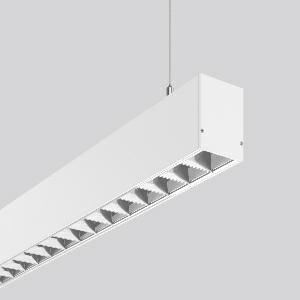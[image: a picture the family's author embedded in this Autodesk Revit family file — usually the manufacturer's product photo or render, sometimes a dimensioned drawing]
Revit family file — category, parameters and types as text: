
# Revit family: less_is_more_50_312341_002_76_e695
name_source: partatom
category: Lighting Fixtures
units: mm (PartAtom-declared; Revit-internal decimal feet)

## family parameters
Cut with Voids When Loaded = No
Host = Face
Light Source = No
Part Type = Normal
Room Calculation Point = No
Round Connector Dimension = Use Diameter
Shared = No

## types (1)
- LESS IS MORE 50 (1 x LED Modul 830, 3950 lm, 3000)
    Apparent Load = 35 VA
    CIE Flux Codes = 95 100 100 63 100
    Color Rendering = 80
    Color Temperature = 3000
    Default Elevation = 1800 mm
    Description = Series: LESS IS MORE 50
Linear pendant luminaire for aesthetically sophisticated lighting. Housing: extruded aluminium profile, powder-coated. End cap aluminium powder-coated. Canopy made of aluminium, powder-coated. Alea optical system: Reflector structure (ABS, Aluminium-coated, highly polished) with integrated diffuser made of non-yellowing plastic (PMMA) opal for glare-free light at the workstation (screen-compliant according to EN 12464-1). Direct 65%, indirect 35% light emission. Controlled separately. Suitable for pendant. 2-point steel cable suspension freely positionable and infinitely height-adjustable. Special lengths available on request. LED unit with integrated converter interchangeable and removable. Suitable for through-wiring. With sensors or as a safety luminaire on request. 
Colour: traffic white, matt (RAL 9016)
Length: 847 mm
Width: 57 mm
Height: 75 mm
Suspension length: 2000 mm
Lamp: LED
Socket: without socket
Colour temperature: 3000K
Colour rendering index (CRI): 80
Light source: LED
Socket lamp2: Without base
Colour temperature: 3000K
System power: 35 W
Rated luminous flux: 3950 lm
Luminous efficiency: 113 lm/W
Control gear: Converter, dimmable, DALI
Control gear: Converter, dimmable, DALI
Protection class: I
Type of protection: IP 20
    Height = 75 mm
    Lamp = 1 x LED Modul 830
    Lamp Light Flux = 3950 lm
    Lamp count = 1
    Length = 847 mm
    Lifetime = 50000 h
    Luminous efficacy = 113 lm/W
    Manufacturer = RZB
    ModVariant = No
    Model = 312341.002.76
    Mounting Place = Ceiling
    Mounting Type = Pendant
    Number of Poles = 1
    OnlyDefault = Yes
    Power Factor = 1
    Product Name = LESS IS MORE 50
    Product group = Pendant LED linear luminaires
    ProductGroupID = 907
    Protection Class = Protection class I
    Protection Degree = IP 20
    RLX_Detail_Level = 1
    RLX_Emergency_Light_Flux = 0 lm
    RLX_Emergency_Type = 0
    RLX_Emergency_Type_DB = No
    RlxData = <blob elided: 37405 chars, md5=40f86997>
    Socket = socket
    Standby Power = 0 W
    System Light Flux = 3950 lm
    System Power = 35 W
    Type Comments = Product without accessories
    Type Image = 312342.002.jpg
    URL = http://relux.com
    VarID = ---
    Voltage = 230 V
    Voltage Range = 220-240 V
    Weight = 0.00 kg
    Width = 57 mm

## geometry (parser evidence)
native form markers: Blend x4, Sweep x14
no freeform markers — native parametric forms only
